# Revit family: Toilet-Lixil-Grohe_Sensia_Electronic_Bidet_Toilet_131886
name_source: partatom
category: Plumbing Fixtures
units: mm (PartAtom-declared; Revit-internal decimal feet)

## family parameters
Cut with Voids When Loaded = No
Enable Cutting in Views = Yes
Host = Face
Maintain Annotation Orientation = No
OmniClass Number = 23.45.55.17
OmniClass Title = Mixing Faucets
Part Type = Normal
Room Calculation Point = No
Round Connector Dimension = Use Diameter
Shared = No

## types (1)
- 131886 - Sensia Electronic Bidet Toilet
    Assembly Code = D2010400
    Brand = GROHE
    CW Connection = Yes
    Cap Finish = Rubber - Grohe - White
    Collection = Sensia
    Default Elevation = 0"
    Description = Electronic Bidet Toilet
    Drain Dimension = 12"
    Finish = Vitreous China - Grohe - Alpine White
    HW Connection = Yes
    Height = 18 3/16"
    Keynote = 22 40 00
    Length = 27 11/16"
    Manufacturer = LIXIL
    Model = 131886
    Product Name = Lixil Grohe Sensia Electronic Bidet Toilet
    Trim Finish = Metal - Grohe - Chrome
    URL = https://www.grohe.us
    Vent Connection = No
    Version = 2023 - v1.0a
    Warranty URL = https://www.grohe.us
    Waste Connection = No
    Width = 15 1/8"

## geometry (parser evidence)
native form markers: Sweep x4
no freeform markers — native parametric forms only
